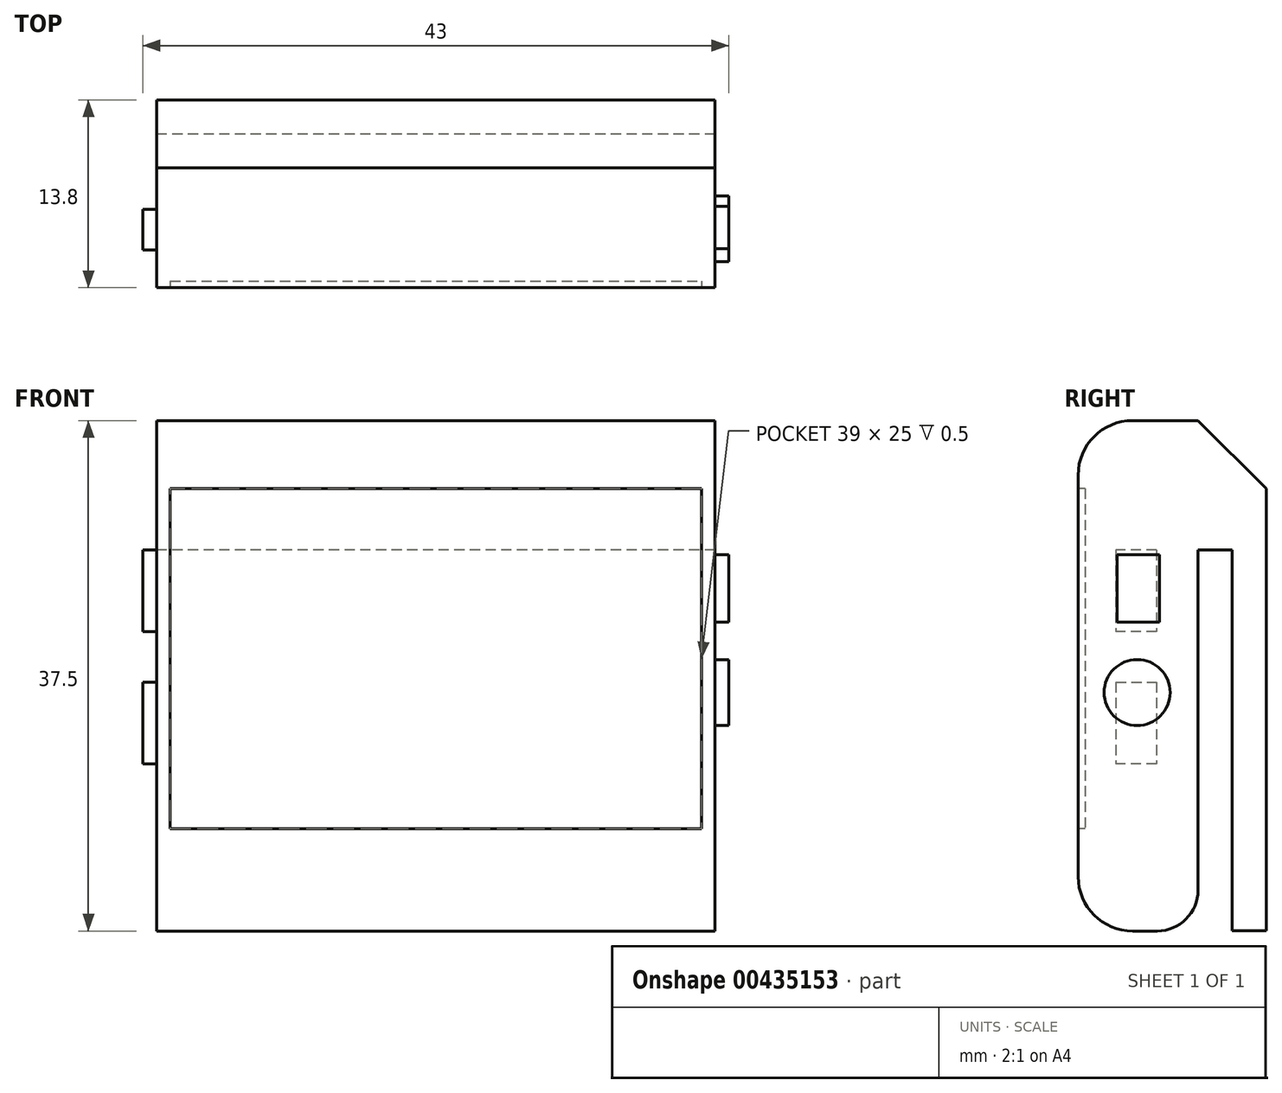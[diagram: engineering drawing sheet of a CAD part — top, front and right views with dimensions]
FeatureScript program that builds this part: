
annotation { "Feature Type Name" : "Feature", "Feature Type Description" : "" }
export const myFeature = defineFeature(function(context is Context, id is Id, definition is map)
    precondition{}
    {
        {
            var Q0;
            Q0=qCreatedBy(makeId("Right.planeOp"),FACE);
            var sketch = newSketch(context, id + "F0", { "sketchPlane" : qUnion([Q0])});
            skLineSegment(sketch, "E0.bottom", {"start": v(-18.47, 14.82) * mm, "end": v(-13.67, 14.82) * mm});
            skLineSegment(sketch, "E0.top", {"start": v(-18.47, -22.68) * mm, "end": v(-16.67, -22.68) * mm});
            skLineSegment(sketch, "E0.left", {"start": v(-22.47, 10.82) * mm, "end": v(-22.47, -18.68) * mm});
            skLineSegment(sketch, "E0.right", {"start": v(-13.67, 14.82) * mm, "end": v(-13.67, -19.68) * mm});
            skLineSegment(sketch, "E1.bottom", {"start": v(-13.67, 9.82) * mm, "end": v(-8.67, 9.82) * mm});
            skLineSegment(sketch, "E1.top", {"start": v(-13.67, 5.32) * mm, "end": v(-8.67, 5.32) * mm});
            skLineSegment(sketch, "E1.left", {"start": v(-13.67, 9.82) * mm, "end": v(-13.67, 5.32) * mm});
            skLineSegment(sketch, "E1.right", {"start": v(-8.67, 9.82) * mm, "end": v(-8.67, 5.32) * mm});
            skLineSegment(sketch, "E2", {"start": v(-8.67, 5.32) * mm, "end": v(-8.67, -22.65) * mm});
            skLineSegment(sketch, "E3", {"start": v(-11.17, 5.32) * mm, "end": v(-11.17, -22.65) * mm});
            skLineSegment(sketch, "E4", {"start": v(-11.17, -22.65) * mm, "end": v(-8.67, -22.65) * mm});
            skLineSegment(sketch, "E5", {"start": v(-13.67, 14.82) * mm, "end": v(-8.67, 9.82) * mm});
            skPoint(sketch, "E6.visualSharp", {"position": v(-22.47, 14.82) * mm});
            skArc(sketch, "E6.filletArc", {"start": v(-18.47, 14.82) * mm, "mid": v(-21.3, 13.65) * mm, "end": v(-22.47, 10.82) * mm});
            skPoint(sketch, "E7.visualSharp", {"position": v(-22.47, -22.68) * mm});
            skArc(sketch, "E7.filletArc", {"start": v(-22.47, -18.68) * mm, "mid": v(-21.3, -21.51) * mm, "end": v(-18.47, -22.68) * mm});
            skPoint(sketch, "E8.visualSharp", {"position": v(-13.67, -22.68) * mm});
            skArc(sketch, "E8.filletArc", {"start": v(-16.67, -22.68) * mm, "mid": v(-14.55, -21.8) * mm, "end": v(-13.67, -19.68) * mm});
            skSolve(sketch);
        }
        {
            var Q0;
            {var subQ1=sQuery(id+"F0.wireOp",EDGE,"E0.bottom");Q0=makeQuery(id+"F0.imprint","IMPRINT",FACE,{"disambiguationData":[TD([[makeQuery(id+"F0.imprint","IMPRINT",EDGE,{"derivedFrom":subQ1}),-1.0]])]});}
            var Q1;
            Q1=makeQuery(id+"F0.imprint","IMPRINT",FACE,{"disambiguationData":[TD([[makeQuery(id+"F0.imprint","IMPRINT",EDGE,{"derivedFrom":sQuery(id+"F0.wireOp",EDGE,"E1.bottom")}),-1.0]])]});
            var Q2;
            {var subQ2=sQuery(id+"F0.wireOp",EDGE,"E1.bottom");Q2=makeQuery(id+"F0.imprint","IMPRINT",FACE,{"disambiguationData":[TD([[makeQuery(id+"F0.imprint","IMPRINT",EDGE,{"derivedFrom":subQ2}),1.0]])]});}
            var Q3;
            {var subQ0=sQuery(id+"F0.wireOp",EDGE,"E2");Q3=makeQuery(id+"F0.imprint","IMPRINT",FACE,{"disambiguationData":[TD([[makeQuery(id+"F0.imprint","IMPRINT",EDGE,{"derivedFrom":subQ0}),-1.0]])]});}
            extrude(context, id + "F1", {"entities" : qUnion([Q0, Q1, Q2, Q3]), "depth" : 41 * mm});
        }
        {
            var Q0;
            Q0=makeQuery(id+"F1.opExtrude","CAP_FACE",FACE,{"disambiguationData":[OSD([sQuery(id+"F0.wireOp",EDGE,"E0.bottom"),sQuery(id+"F0.wireOp",EDGE,"E0.top"),sQuery(id+"F0.wireOp",EDGE,"E0.left"),sQuery(id+"F0.wireOp",EDGE,"E0.right"),sQuery(id+"F0.wireOp",EDGE,"E1.top"),sQuery(id+"F0.wireOp",EDGE,"E1.right"),sQuery(id+"F0.wireOp",EDGE,"E2"),sQuery(id+"F0.wireOp",EDGE,"E3"),sQuery(id+"F0.wireOp",EDGE,"E4"),sQuery(id+"F0.wireOp",EDGE,"E5"),sQuery(id+"F0.wireOp",EDGE,"E6.filletArc"),sQuery(id+"F0.wireOp",EDGE,"E7.filletArc"),sQuery(id+"F0.wireOp",EDGE,"E8.filletArc")])],"isStart":false});
            var sketch = newSketch(context, id + "F2", { "sketchPlane" : qUnion([Q0])});
            skLineSegment(sketch, "E9.bottom", {"start": v(-19.6, 4.97) * mm, "end": v(-16.5, 4.97) * mm});
            skLineSegment(sketch, "E9.top", {"start": v(-19.6, 0) * mm, "end": v(-16.5, 0) * mm});
            skLineSegment(sketch, "E9.left", {"start": v(-19.6, 4.97) * mm, "end": v(-19.6, 0) * mm});
            skLineSegment(sketch, "E9.right", {"start": v(-16.5, 4.97) * mm, "end": v(-16.5, 0) * mm});
            skCircle(sketch, "E10", {"center": v(-18.14, -5.16) * mm, "radius": 2.42 * mm});
            skSolve(sketch);
        }
        {
            var Q0;
            Q0 = qSketchRegion(id + "F2", true);
            extrude(context, id + "F3", {"entities" : qUnion([Q0]), "operationType" : NewBodyOperationType.ADD, "depth" : 1 * mm});
        }
        {
            var Q0;
            Q0=makeQuery(id+"F1.opExtrude","CAP_FACE",FACE,{"disambiguationData":[OSD([sQuery(id+"F0.wireOp",EDGE,"E0.bottom"),sQuery(id+"F0.wireOp",EDGE,"E0.top"),sQuery(id+"F0.wireOp",EDGE,"E0.left"),sQuery(id+"F0.wireOp",EDGE,"E0.right"),sQuery(id+"F0.wireOp",EDGE,"E1.top"),sQuery(id+"F0.wireOp",EDGE,"E1.right"),sQuery(id+"F0.wireOp",EDGE,"E2"),sQuery(id+"F0.wireOp",EDGE,"E3"),sQuery(id+"F0.wireOp",EDGE,"E4"),sQuery(id+"F0.wireOp",EDGE,"E5"),sQuery(id+"F0.wireOp",EDGE,"E6.filletArc"),sQuery(id+"F0.wireOp",EDGE,"E7.filletArc"),sQuery(id+"F0.wireOp",EDGE,"E8.filletArc")])],"isStart":true});
            var sketch = newSketch(context, id + "F4", { "sketchPlane" : qUnion([Q0])});
            skLineSegment(sketch, "E11.bottom", {"start": v(16.7, 5.31) * mm, "end": v(19.7, 5.31) * mm});
            skLineSegment(sketch, "E11.top", {"start": v(16.7, -10.4) * mm, "end": v(19.7, -10.4) * mm});
            skLineSegment(sketch, "E11.left", {"start": v(16.7, 5.31) * mm, "end": v(16.7, -0.69) * mm});
            skLineSegment(sketch, "E11.right", {"start": v(19.7, 5.31) * mm, "end": v(19.7, -0.69) * mm});
            skLineSegment(sketch, "E12", {"start": v(16.7, -0.69) * mm, "end": v(19.7, -0.69) * mm});
            skLineSegment(sketch, "E13", {"start": v(19.7, -4.4) * mm, "end": v(16.7, -4.4) * mm});
            skLineSegment(sketch, "E14.trimOffspring", {"start": v(16.7, -4.4) * mm, "end": v(16.7, -10.4) * mm});
            skLineSegment(sketch, "E15.trimOffspring", {"start": v(19.7, -4.4) * mm, "end": v(19.7, -10.4) * mm});
            skSolve(sketch);
        }
        {
            var Q0;
            Q0=makeQuery(id+"F4.imprint","IMPRINT",FACE,{"disambiguationData":[TD([[makeQuery(id+"F4.imprint","IMPRINT",EDGE,{"derivedFrom":sQuery(id+"F4.wireOp",EDGE,"E11.bottom")}),-1.0]])]});
            var Q1;
            Q1=makeQuery(id+"F4.imprint","IMPRINT",FACE,{"disambiguationData":[TD([[makeQuery(id+"F4.imprint","IMPRINT",EDGE,{"derivedFrom":sQuery(id+"F4.wireOp",EDGE,"E11.top")}),1.0]])]});
            extrude(context, id + "F5", {"entities" : qUnion([Q0, Q1]), "operationType" : NewBodyOperationType.ADD, "depth" : 1 * mm});
        }
        {
            var Q0;
            Q0=makeQuery(id+"F1.opExtrude","SWEPT_FACE",FACE,{"disambiguationData":[OSD([sQuery(id+"F0.wireOp",EDGE,"E0.left")])]});
            var sketch = newSketch(context, id + "F6", { "sketchPlane" : qUnion([Q0])});
            skLineSegment(sketch, "E16.bottom", {"start": v(1, 9.82) * mm, "end": v(40, 9.82) * mm});
            skLineSegment(sketch, "E16.top", {"start": v(1, -15.18) * mm, "end": v(40, -15.18) * mm});
            skLineSegment(sketch, "E16.left", {"start": v(1, 9.82) * mm, "end": v(1, -15.18) * mm});
            skLineSegment(sketch, "E16.right", {"start": v(40, 9.82) * mm, "end": v(40, -15.18) * mm});
            skSolve(sketch);
        }
        {
            var Q0;
            Q0=makeQuery(id+"F6.imprint","IMPRINT",FACE,{"disambiguationData":[TD([[makeQuery(id+"F6.imprint","IMPRINT",EDGE,{"derivedFrom":sQuery(id+"F6.wireOp",EDGE,"E16.bottom")}),-1.0]])]});
            extrude(context, id + "F7", {"entities" : qUnion([Q0]), "operationType" : NewBodyOperationType.REMOVE, "oppositeDirection" : true, "depth" : 0.5 * mm});
        }
    });
